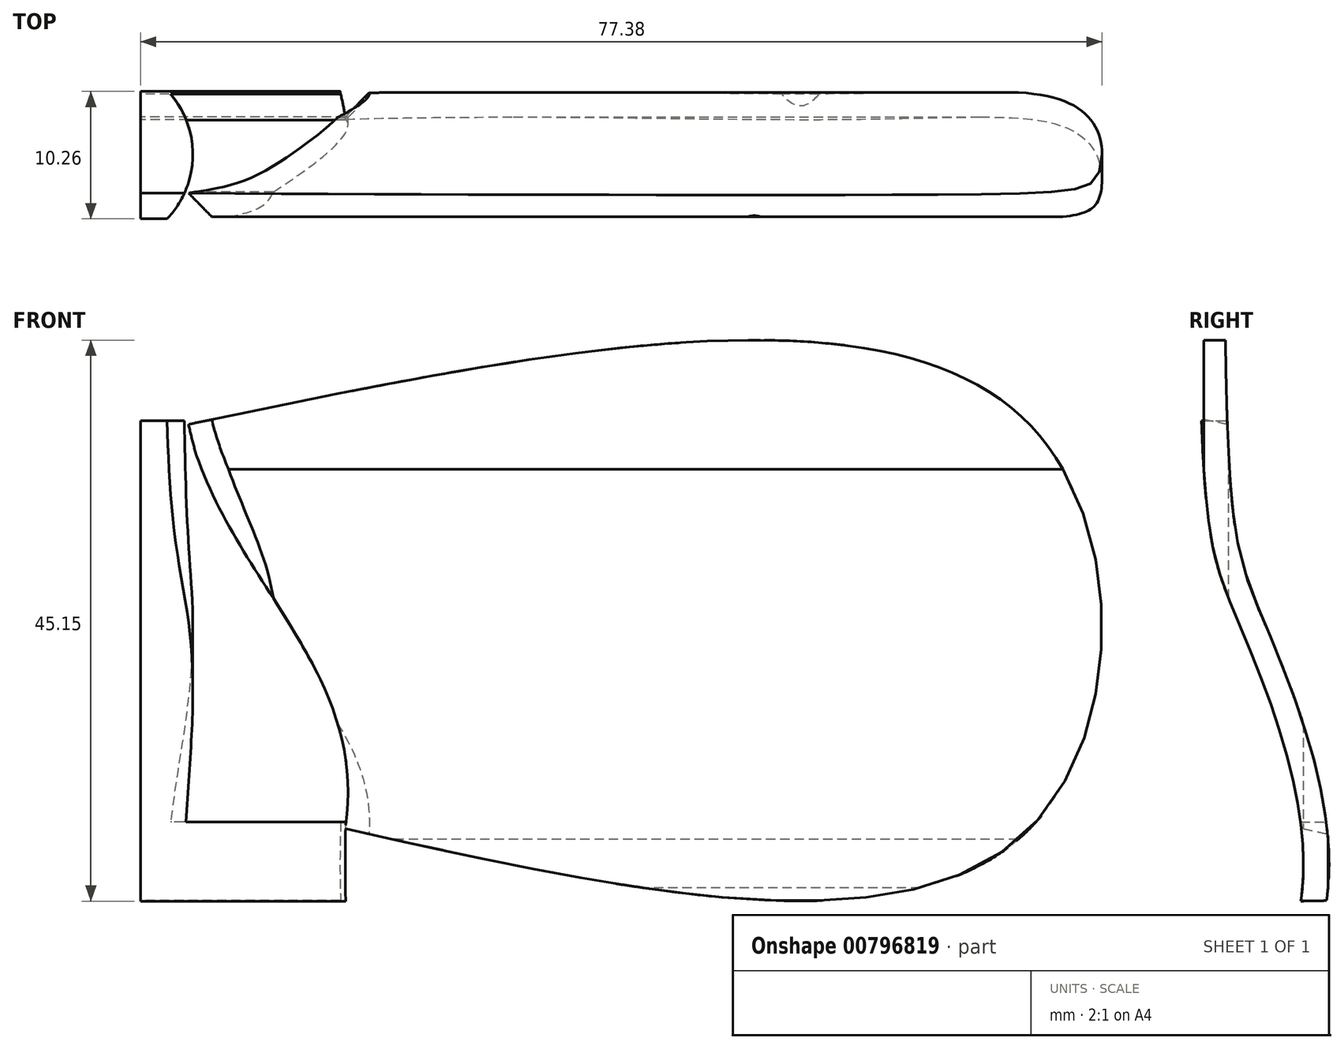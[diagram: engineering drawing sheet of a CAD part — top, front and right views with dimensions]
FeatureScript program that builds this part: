
annotation { "Feature Type Name" : "Feature", "Feature Type Description" : "" }
export const myFeature = defineFeature(function(context is Context, id is Id, definition is map)
    precondition{}
    {
        {
            var Q0;
            Q0=qCreatedBy(makeId("Top.planeOp"),FACE);
            var sketch = newSketch(context, id + "F0", { "sketchPlane" : qUnion([Q0])});
            skCircle(sketch, "E0", {"center": v(0, 0) * mm, "radius": 20 * mm});
            skSolve(sketch);
        }
        {
            var Q0;
            Q0=makeQuery(id+"F0.imprint","IMPRINT",FACE,{"disambiguationData":[TD([[makeQuery(id+"F0.imprint","IMPRINT",EDGE,{"derivedFrom":sQuery(id+"F0.wireOp",EDGE,"E0")}),1.0]])]});
            extrude(context, id + "F1", {"entities" : qUnion([Q0]), "depth" : 42.1 * mm, "offsetDistance" : 25 * mm});
        }
        {
            var Q0;
            Q0=qCreatedBy(makeId("Top.planeOp"),FACE);
            var sketch = newSketch(context, id + "F2", { "sketchPlane" : qUnion([Q0])});
            skCircle(sketch, "E1", {"center": v(0, 0) * mm, "radius": 7.5 * mm});
            skSolve(sketch);
        }
        {
            var Q0;
            Q0 = qSketchRegion(id + "F2", true);
            extrude(context, id + "F3", {"entities" : qUnion([Q0]), "operationType" : NewBodyOperationType.ADD, "depth" : 74.4 * mm, "offsetDistance" : 25 * mm});
        }
        {
            var Q0;
            Q0=qCreatedBy(makeId("Front.planeOp"),FACE);
            var sketch = newSketch(context, id + "F4", { "sketchPlane" : qUnion([Q0])});
            skPoint(sketch, "E2", {"position": v(-19.87, 42.06) * mm});
            skPoint(sketch, "E3", {"position": v(-7.37, 74.43) * mm});
            skFitSpline(sketch, "E4", {"points": [v(-19.87, 42.06) * mm, v(-7.37, 74.43) * mm], "startDerivative": vector(-4.15, 41.23) * mm, "endDerivative": vector(4.57, 36.77) * mm});
            skSolve(sketch);
        }
        {
            var Q0;
            Q0=makeQuery(id+"F1.opExtrude","CAP_FACE",FACE,{"disambiguationData":[OSD([sQuery(id+"F0.wireOp",EDGE,"E0")])],"isStart":false});
            var Q1;
            Q1=sQuery(id+"F4.wireOp",EDGE,"E4");
            var Q2;
            Q2=makeQuery(id+"F3.opExtrude","SWEPT_FACE",FACE,{"disambiguationData":[OSD([sQuery(id+"F2.wireOp",EDGE,"E1")])]});
            revolve(context, id + "F5", {"bodyType" : ToolBodyType.SURFACE, "operationType" : NewBodyOperationType.ADD, "surfaceOperationType" : NewSurfaceOperationType.NEW, "entities" : qUnion([Q0]), "surfaceEntities" : qUnion([Q1]), "axis" : qUnion([Q2]), "revolveType" : RevolveType.FULL});
        }
        {
            var Q0;
            Q0=makeQuery(id+"F1.opExtrude","CAP_EDGE",EDGE,{"disambiguationData":[OSD([sQuery(id+"F0.wireOp",EDGE,"E0")])],"isStart":false});
            cPlane(context, id + "F6", {"entities" : qUnion([Q0]), "cplaneType" : CPlaneType.LINE_ANGLE, "offset" : 25 * mm, "angle" : 90 * degree, "oppositeDirection" : true, "width" : 150 * mm, "height" : 150 * mm});
        }
        {
            var Q0;
            Q0=qCreatedBy(id+"F6.planeOp",FACE);
            var sketch = newSketch(context, id + "F7", { "sketchPlane" : qUnion([Q0])});
            skPoint(sketch, "E5", {"position": v(7.06, 74.09) * mm});
            skPoint(sketch, "E6", {"position": v(19.76, 41.57) * mm});
            skPoint(sketch, "E7", {"position": v(74.85, 41.57) * mm});
            skPoint(sketch, "E8", {"position": v(74.85, 74.09) * mm});
            skFitSpline(sketch, "E9", {"points": [v(7.06, 74.09) * mm, v(74.85, 74.09) * mm, v(74.85, 41.57) * mm, v(19.76, 41.57) * mm], "startDerivative": vector(219.59, 45.83) * mm, "endDerivative": vector(-194.8, 43.42) * mm});
            skFitSpline(sketch, "E10", {"points": [v(19.76, 41.57) * mm, v(7.06, 74.09) * mm], "startDerivative": vector(6.15, 38.5) * mm, "endDerivative": vector(-9.22, 37.48) * mm});
            skSolve(sketch);
        }
        {
            var Q0;
            Q0=makeQuery(id+"F7.imprint","IMPRINT",FACE,{"disambiguationData":[TD([[makeQuery(id+"F7.imprint","IMPRINT",EDGE,{"derivedFrom":sQuery(id+"F7.wireOp",EDGE,"E9")}),-1.0]])]});
            extrude(context, id + "F8", {"entities" : qUnion([Q0]), "operationType" : NewBodyOperationType.ADD, "depth" : 5 * mm, "offsetDistance" : 25 * mm, "hasSecondDirection" : true, "secondDirectionOppositeDirection" : true, "secondDirectionDepth" : 5 * mm});
        }
        {
            var Q0;
            Q0=makeQuery(id+"F8.opExtrude","CAP_EDGE",EDGE,{"disambiguationData":[OSD([sQuery(id+"F7.wireOp",EDGE,"E10")])],"isStart":true});
            var Q1;
            Q1=makeQuery(id+"F8.opExtrude","CAP_EDGE",EDGE,{"disambiguationData":[OSD([sQuery(id+"F7.wireOp",EDGE,"E10")])],"isStart":false});
            chamfer(context, id + "F9", {"entities" : qUnion([Q0, Q1]), "width" : 2 * mm, "tangentPropagation" : true});
        }
        {
            var Q0;
            Q0=qCreatedBy(makeId("Right.planeOp"),FACE);
            var sketch = newSketch(context, id + "F10", { "sketchPlane" : qUnion([Q0])});
            skFitSpline(sketch, "E11", {"points": [v(-3.25, 80.92) * mm, v(0, 57.88) * mm, v(4.88, 35.78) * mm], "startDerivative": vector(1.2, -95.82) * mm, "endDerivative": vector(-6.76, -45.97) * mm});
            skFitSpline(sketch, "E12", {"points": [v(-5.32, 80.88) * mm, v(-2.06, 57.84) * mm, v(2.81, 35.74) * mm], "startDerivative": vector(1.2, -95.82) * mm, "endDerivative": vector(-6.76, -45.97) * mm});
            skLineSegment(sketch, "E13", {"start": v(-5.32, 80.88) * mm, "end": v(-3.25, 80.92) * mm});
            skLineSegment(sketch, "E14", {"start": v(2.81, 35.74) * mm, "end": v(4.88, 35.78) * mm});
            skSolve(sketch);
        }
        {
            var Q0;
            Q0=makeQuery(id+"F10.imprint","IMPRINT",FACE,{"disambiguationData":[TD([[makeQuery(id+"F10.imprint","IMPRINT",EDGE,{"derivedFrom":sQuery(id+"F10.wireOp",EDGE,"E11")}),-1.0]])]});
            extrude(context, id + "F11", {"entities" : qUnion([Q0]), "operationType" : NewBodyOperationType.INTERSECT, "depth" : 190.6 * mm, "offsetDistance" : 25 * mm, "hasSecondDirection" : true, "secondDirectionOppositeDirection" : false, "secondDirectionDepth" : 3.3 * mm});
        }
    });
